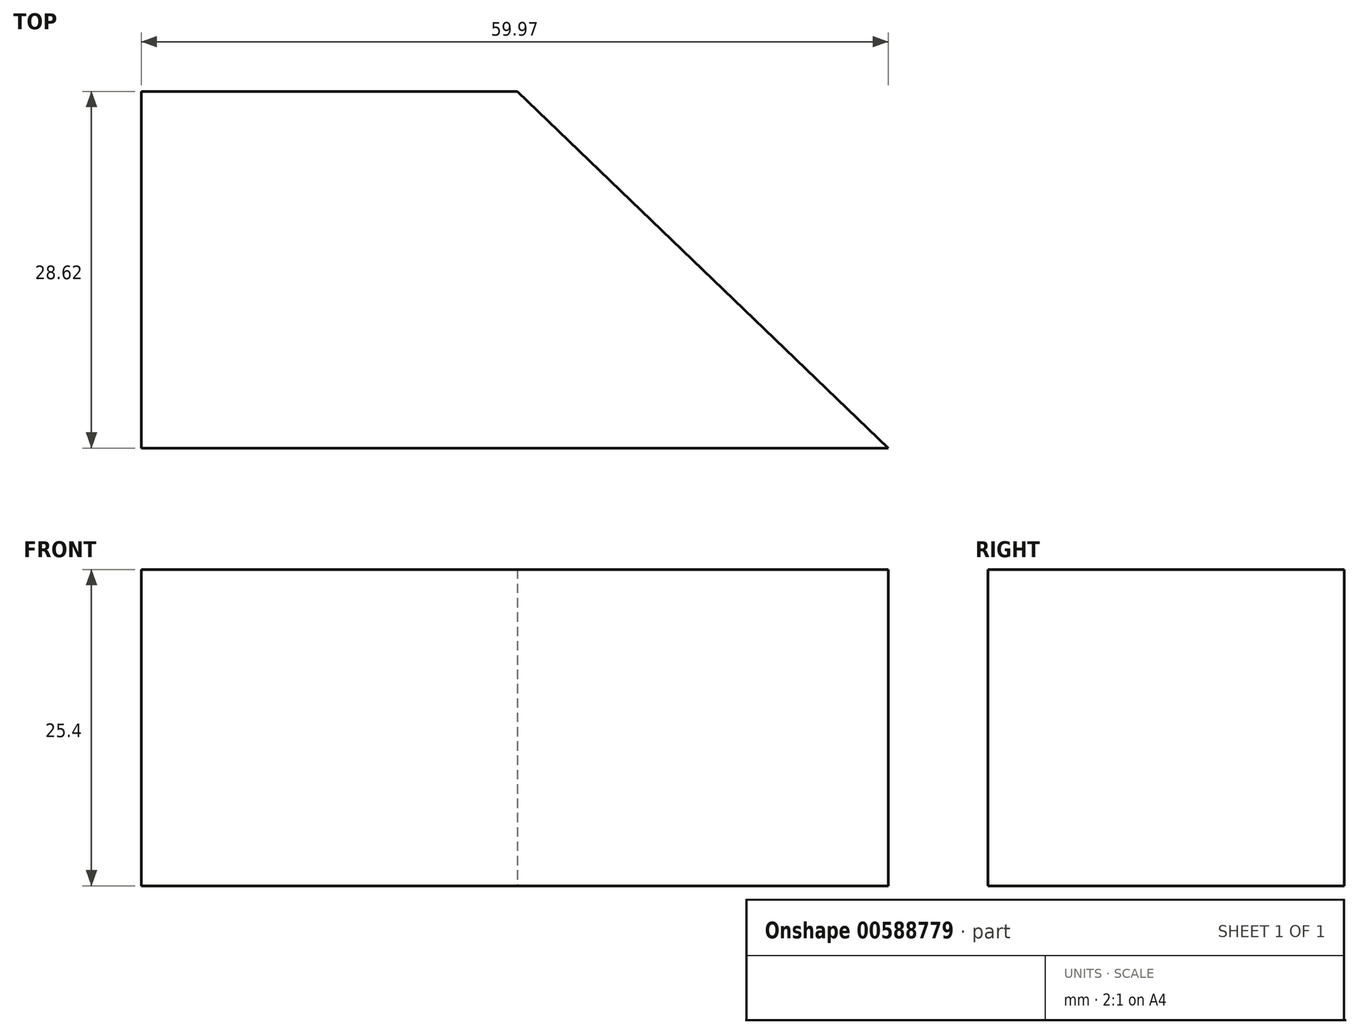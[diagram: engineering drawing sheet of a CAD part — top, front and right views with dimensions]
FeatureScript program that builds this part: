
annotation { "Feature Type Name" : "Feature", "Feature Type Description" : "" }
export const myFeature = defineFeature(function(context is Context, id is Id, definition is map)
    precondition{}
    {
        {
            var Q0;
            Q0=qCreatedBy(makeId("Top.planeOp"),FACE);
            var sketch = newSketch(context, id + "F0", { "sketchPlane" : qUnion([Q0])});
            skLineSegment(sketch, "E0", {"start": v(0, 0) * mm, "end": v(-29.8, 28.62) * mm});
            skLineSegment(sketch, "E1", {"start": v(-29.8, 28.62) * mm, "end": v(-59.97, 28.62) * mm});
            skLineSegment(sketch, "E2", {"start": v(-59.97, 28.62) * mm, "end": v(-59.97, 0) * mm});
            skLineSegment(sketch, "E3", {"start": v(-59.97, 0) * mm, "end": v(0, 0) * mm});
            skSolve(sketch);
        }
        {
            var Q0;
            Q0 = qSketchRegion(id + "F0", true);
            extrude(context, id + "F1", {"entities" : qUnion([Q0]), "depth" : 25.4 * mm, "offsetDistance" : 25.4 * mm});
        }
    });
